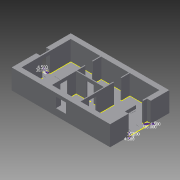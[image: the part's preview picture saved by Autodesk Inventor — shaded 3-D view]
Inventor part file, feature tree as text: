
AUTODESK INVENTOR PART (.ipt)
format: ipt  version: 2014 (Build 180170000, 170)  size: 494,592 bytes
history: native  units: in
note: dims shown in document units (in); Inventor stores cm internally (conversion verified against a paired STEP export)
features: extrude x10, sketch x9, projected_geometry x6, other x2
ambient origin geometry x8: Origin, YZ Plane, XZ Plane, XY Plane, X Axis, Y Axis, Z Axis, Center Point
bodies: Solid1 (feature_tree)
feature tree (27):
  extrude  "Extrusion1"  Depth=24.0in
  extrude  "Extrusion2"  Depth=4.5in
  extrude  "Extrusion3"  Depth=168.0in
  extrude  "Extrusion5"  Depth=36.0in
  extrude  "Extrusion6"  Depth=4.5in
  extrude  "Extrusion7"  Depth=40.875in
  extrude  "Extrusion8"  Depth=36.0in
  extrude  "Extrusion9"  Depth=168.0in
  other  "Open Doors"
  extrude  "Extrusion11"  Depth=480.0in
  extrude  "Roof Vent"  Depth=24.0in
  sketch  "Sketch1"  dims[d0=480.0in d2=288.0in d3=24.0in d4=24.0in]
  sketch  "Sketch2"  dims[d6=4.5in d8=4.5in d9=4.5in]
  sketch  "Sketch3"  dims[d10=24.0in d12=168.0in]
  projected_geometry  "Projected Loop1"
  projected_geometry  "Projected Loop2"
  projected_geometry  "Projected Loop3"
  sketch  "Sketch5"  dims[d13=40.875in d14=36.0in]
  projected_geometry  "Projected Loop4"
  sketch  "Sketch6"  dims[d15=168.0in d16=4.5in d17=4.5in]
  projected_geometry  "Projected Loop5"
  sketch  "Sketch7"  dims[d18=40.875in d19=40.875in]
  sketch  "Sketch8"  dims[d20=36.0in d21=36.0in]
  sketch  "Sketch9"  dims[d22=480.0in d23=24.0in d24=168.0in]
  projected_geometry  "Projected Loop6"
  sketch  "Sketch11"  dims[d25=72.0in d26=480.0in d27=24.0in d28=4.5in d29=96.0in d30=0.0in d31=48.0in d33=48.0in d34=32.0in d35=96.0in d36=0.0in d37=16.0in d38=0.0in d43=1.0in d44=0.0in d46=6.0in d47=6.0in d48=1.0in d49=0.0in d50=1.0in d51=0.0in d52=18.0in d53=18.0in d54=6.0in d55=6.0in d56=1.0in d57=0.0in d58=1.0in d59=0.0in d60=36.0in d62=4.5in d63=36.0in d64=4.5in d65=36.0in d66=4.5in d67=224.0in d68=60.0in d69=46.0in d70=46.0in d71=1.0in d72=0.0in d73=77.9528in d74=25.9843in d75=24.0in d76=24.0in d79=6.0in d80=6.0in d81=12.0in d82=12.0in d83=12.0in d84=12.0in d85=12.0in d86=12.0in d87=12.0in d88=12.0in d89=12.0in d91=205.1181in d92=12.0in d93=12.0in d94=83.0709in d95=96.063in d96=96.063in d97=83.0709in d98=240.1575in d99=12.0in d100=383.8583in d101=83.0709in d102=12.0in d103=383.8583in d104=205.1181in d108=12.0in d109=12.0in d110=12.0in d111=6.0in d113=12.0in d114=12.0in d115=12.0in d116=1.0in d117=0.0in]
  other  "Instruments"
